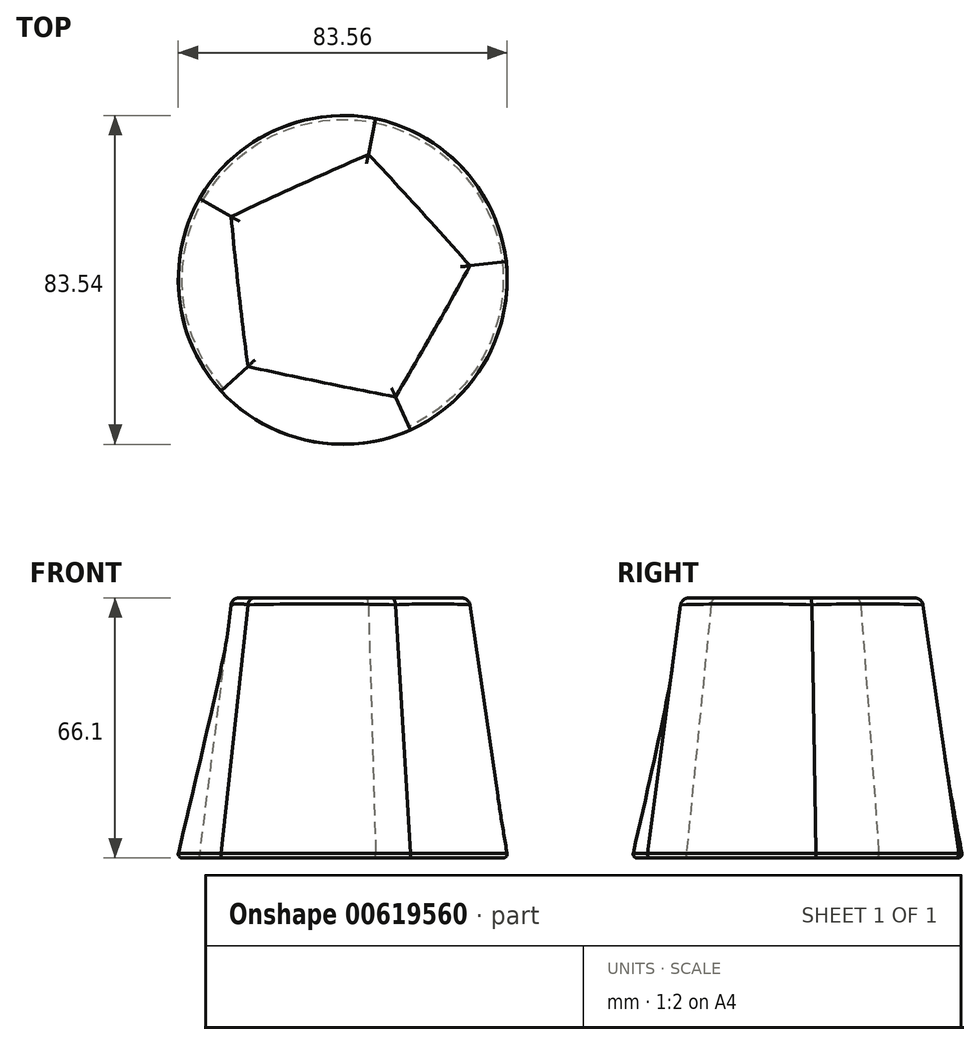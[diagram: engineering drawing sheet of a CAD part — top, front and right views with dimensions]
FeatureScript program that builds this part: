
annotation { "Feature Type Name" : "Feature", "Feature Type Description" : "" }
export const myFeature = defineFeature(function(context is Context, id is Id, definition is map)
    precondition{}
    {
        {
            var Q0;
            Q0=qCreatedBy(makeId("Top.planeOp"),FACE);
            var Q1;
            Q1 = qBodyType(qCreatedBy(id + "F1" ,EDGE), BodyType.WIRE);
            cPlane(context, id + "F0", {"entities" : qUnion([Q0, Q1]), "cplaneType" : CPlaneType.OFFSET, "offset" : 66.1 * mm, "width" : 152.4 * mm, "height" : 152.4 * mm});
        }
        {
            var Q0;
            Q0=qCreatedBy(makeId("Top.planeOp"),FACE);
            var sketch = newSketch(context, id + "F1", { "sketchPlane" : qUnion([Q0])});
            skCircle(sketch, "E0", {"center": v(0, 0) * mm, "radius": 42 * mm});
            skSolve(sketch);
        }
        {
            var Q0;
            Q0=qCreatedBy(id+"F0.planeOp",FACE);
            var sketch = newSketch(context, id + "F2", { "sketchPlane" : qUnion([Q0])});
            skCircle(sketch, "E1.cCircle", {"center": v(0, 0) * mm, "radius": 26.14 * mm, "construction": true});
            skLineSegment(sketch, "E1.0", {"start": v(-28.1, 15.97) * mm, "end": v(6.5, 31.66) * mm});
            skLineSegment(sketch, "E1.1", {"start": v(6.5, 31.66) * mm, "end": v(32.12, 3.6) * mm});
            skLineSegment(sketch, "E1.2", {"start": v(32.12, 3.6) * mm, "end": v(13.35, -29.43) * mm});
            skLineSegment(sketch, "E1.3", {"start": v(13.35, -29.43) * mm, "end": v(-23.87, -21.79) * mm});
            skLineSegment(sketch, "E1.4", {"start": v(-23.87, -21.79) * mm, "end": v(-28.1, 15.97) * mm});
            skPoint(sketch, "E1.0.midPoint", {"position": v(-10.8, 23.81) * mm});
            skSolve(sketch);
        }
        {
            var Q0;
            Q0=makeQuery(id+"F2.imprint","IMPRINT",FACE,{"disambiguationData":[TD([[makeQuery(id+"F2.imprint","IMPRINT",EDGE,{"derivedFrom":sQuery(id+"F2.wireOp",EDGE,"E1.0")}),-1.0]])]});
            var Q1;
            Q1=makeQuery(id+"F1.imprint","IMPRINT",FACE,{"disambiguationData":[TD([[makeQuery(id+"F1.imprint","IMPRINT",EDGE,{"derivedFrom":sQuery(id+"F1.wireOp",EDGE,"E0")}),1.0]])]});
            loft(context, id + "F3", {"sheetProfilesArray" : [{ "sheetProfileEntities" : qUnion([Q0]) }, { "sheetProfileEntities" : qUnion([Q1]) }]});
        }
        {
            var Q0;
            Q0=makeQuery(id+"F3.opLoft","CAP_FACE",FACE,{"disambiguationData":[OSD([makeQuery(id+"F2.imprint","IMPRINT",FACE,{"disambiguationData":[TD([[makeQuery(id+"F2.imprint","IMPRINT",EDGE,{"derivedFrom":sQuery(id+"F2.wireOp",EDGE,"E1.0")}),-1.0]])]})])],"isStart":true});
            fillet(context, id + "F4", {"entities" : qUnion([Q0]), "radius" : 2 * mm, "tangentPropagation" : true, "allowEdgeOverflow" : false});
        }
        {
            var Q0;
            Q0=makeQuery(id+"F3.opLoft","CAP_FACE",FACE,{"disambiguationData":[OSD([makeQuery(id+"F1.imprint","IMPRINT",FACE,{"disambiguationData":[TD([[makeQuery(id+"F1.imprint","IMPRINT",EDGE,{"derivedFrom":sQuery(id+"F1.wireOp",EDGE,"E0")}),1.0]])]})])],"isStart":true});
            fillet(context, id + "F5", {"entities" : qUnion([Q0]), "radius" : 1 * mm, "tangentPropagation" : true, "allowEdgeOverflow" : false});
        }
    });
